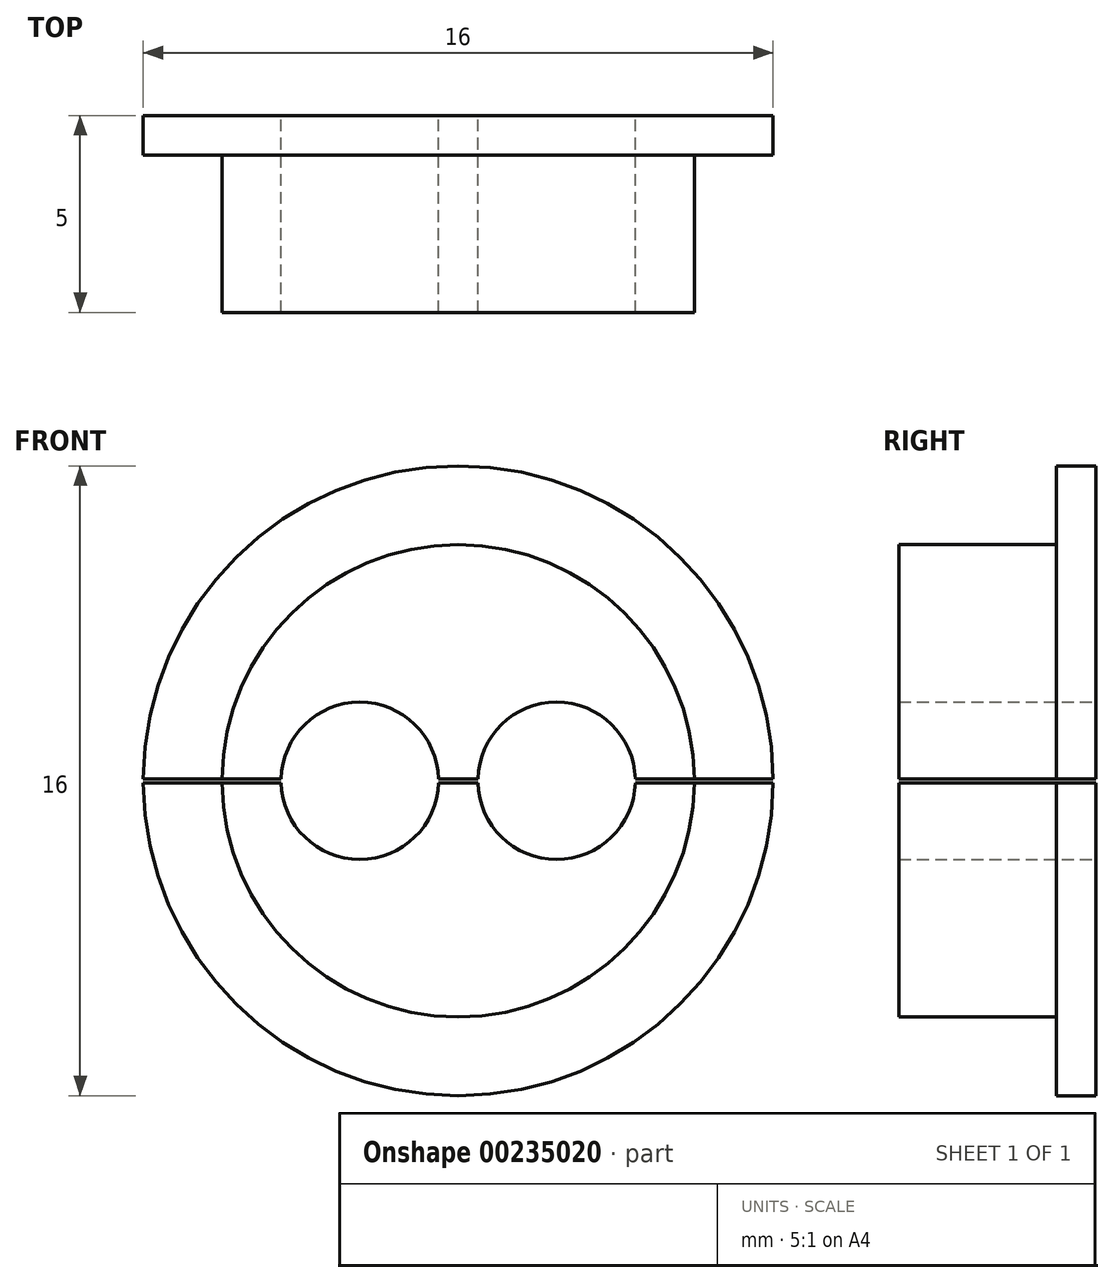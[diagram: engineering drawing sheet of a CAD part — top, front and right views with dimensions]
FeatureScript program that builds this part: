
annotation { "Feature Type Name" : "Feature", "Feature Type Description" : "" }
export const myFeature = defineFeature(function(context is Context, id is Id, definition is map)
    precondition{}
    {
        {
            var Q0;
            Q0=qCreatedBy(makeId("Front.planeOp"),FACE);
            var sketch = newSketch(context, id + "F0", { "sketchPlane" : qUnion([Q0])});
            skCircle(sketch, "E0", {"center": v(0, 0) * mm, "radius": 6 * mm});
            skCircle(sketch, "E1", {"center": v(-2.5, 0) * mm, "radius": 2 * mm});
            skLineSegment(sketch, "E2", {"start": v(0, 0) * mm, "end": v(0, 7.85) * mm, "construction": true});
            skCircle(sketch, "E3.MirrorC", {"center": v(2.5, 0) * mm, "radius": 2 * mm});
            skSolve(sketch);
        }
        {
            var Q0;
            Q0 = qSketchRegion(id + "F0", true);
            extrude(context, id + "F1", {"entities" : qUnion([Q0]), "depth" : 5 * mm});
        }
        {
            var Q0;
            Q0=makeQuery(id+"F1.opExtrude","CAP_FACE",FACE,{"disambiguationData":[OSD([sQuery(id+"F0.wireOp",EDGE,"E0"),sQuery(id+"F0.wireOp",EDGE,"E1"),sQuery(id+"F0.wireOp",EDGE,"E3.MirrorC")])],"isStart":true});
            var sketch = newSketch(context, id + "F2", { "sketchPlane" : qUnion([Q0])});
            skCircle(sketch, "E4", {"center": v(0, 0) * mm, "radius": 8 * mm});
            skSolve(sketch);
        }
        {
            var Q0;
            Q0=makeQuery(id+"F2.imprint","IMPRINT",FACE,{"disambiguationData":[TD([[makeQuery(id+"F2.imprint","IMPRINT",EDGE,{"derivedFrom":sQuery(id+"F2.wireOp",EDGE,"E4")}),1.0]])]});
            extrude(context, id + "F3", {"entities" : qUnion([Q0]), "operationType" : NewBodyOperationType.ADD, "oppositeDirection" : true, "depth" : 1 * mm});
        }
        {
            var Q0;
            Q0=qCreatedBy(makeId("Front.planeOp"),FACE);
            var sketch = newSketch(context, id + "F4", { "sketchPlane" : qUnion([Q0])});
            skLineSegment(sketch, "E5.bottom", {"start": v(15.02, 0.05) * mm, "end": v(-14.98, 0.05) * mm});
            skLineSegment(sketch, "E5.top", {"start": v(15.02, -0.05) * mm, "end": v(-14.98, -0.05) * mm});
            skLineSegment(sketch, "E5.left", {"start": v(15.02, 0.05) * mm, "end": v(15.02, -0.05) * mm});
            skLineSegment(sketch, "E5.right", {"start": v(-14.98, 0.05) * mm, "end": v(-14.98, -0.05) * mm});
            skPoint(sketch, "E5.middle", {"position": v(0.02, 0) * mm});
            skSolve(sketch);
        }
        {
            var Q0;
            Q0 = qSketchRegion(id + "F4", true);
            extrude(context, id + "F5", {"entities" : qUnion([Q0]), "operationType" : NewBodyOperationType.REMOVE, "endBound" : BoundingType.THROUGH_ALL, "oppositeDirection" : true, "depth" : 25 * mm, "hasSecondDirection" : true, "secondDirectionBound" : SecondDirectionBoundingType.THROUGH_ALL, "secondDirectionOppositeDirection" : false, "secondDirectionDepth" : 25 * mm});
        }
    });
